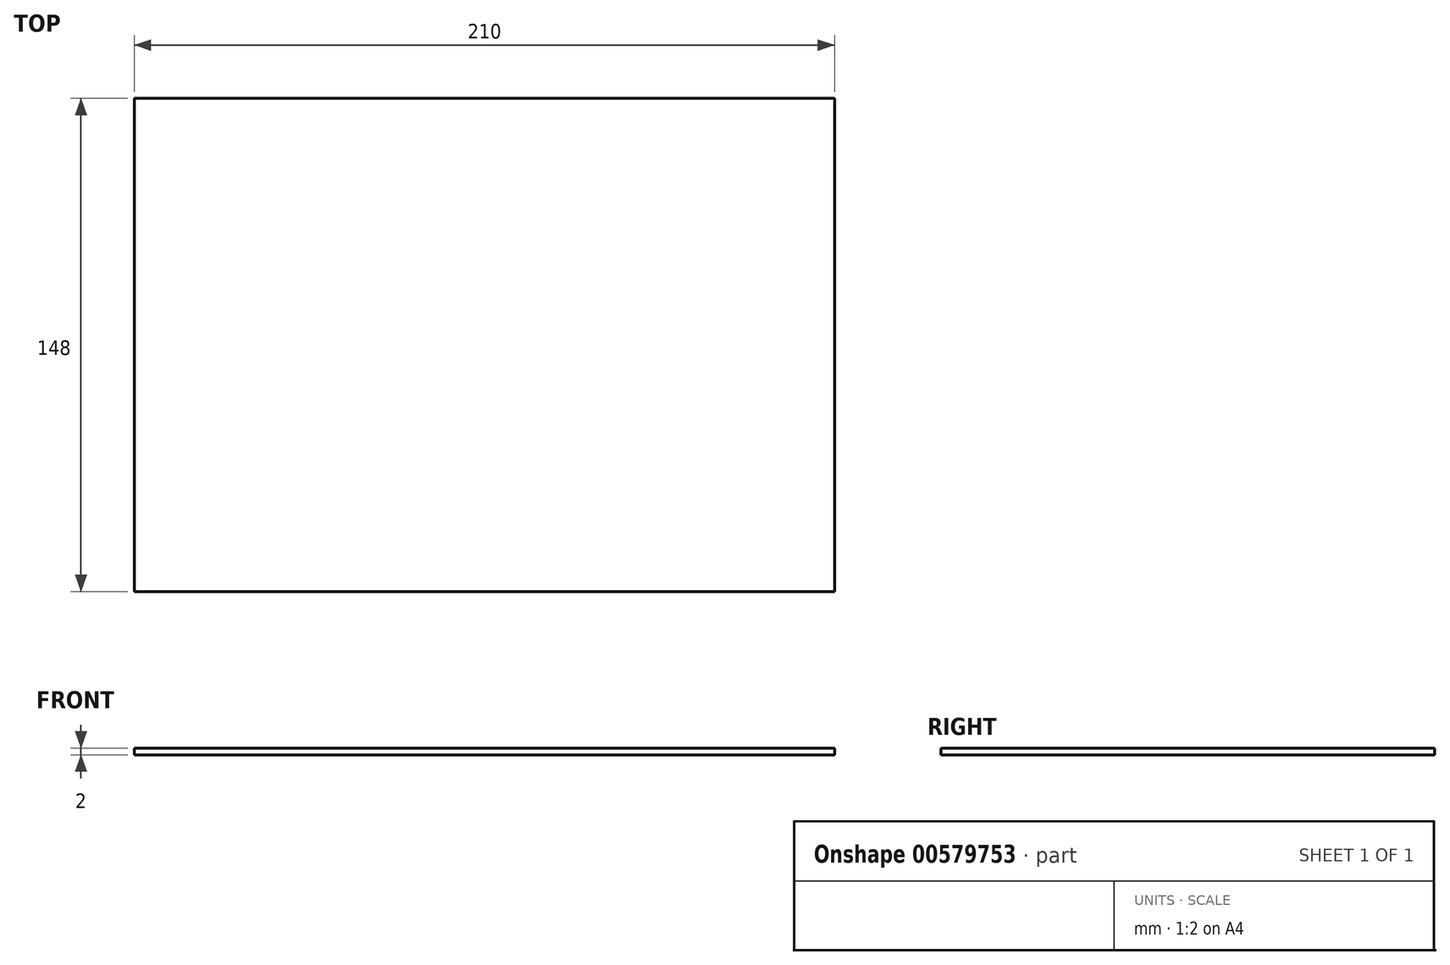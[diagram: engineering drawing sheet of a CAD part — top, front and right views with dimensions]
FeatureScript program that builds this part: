
annotation { "Feature Type Name" : "Feature", "Feature Type Description" : "" }
export const myFeature = defineFeature(function(context is Context, id is Id, definition is map)
    precondition{}
    {
        {
            var Q0;
            Q0=qCreatedBy(makeId("Top.planeOp"),FACE);
            var sketch = newSketch(context, id + "F0", { "sketchPlane" : qUnion([Q0])});
            skLineSegment(sketch, "E0.bottom", {"start": v(-51.26, 44.59) * mm, "end": v(-261.26, 44.59) * mm});
            skLineSegment(sketch, "E0.top", {"start": v(-51.26, 192.59) * mm, "end": v(-261.26, 192.59) * mm});
            skLineSegment(sketch, "E0.left", {"start": v(-51.26, 44.59) * mm, "end": v(-51.26, 192.59) * mm});
            skLineSegment(sketch, "E0.right", {"start": v(-261.26, 44.59) * mm, "end": v(-261.26, 192.59) * mm});
            skSolve(sketch);
        }
        {
            var Q0;
            Q0 = qSketchRegion(id + "F0", true);
            extrude(context, id + "F1", {"entities" : qUnion([Q0]), "depth" : 2 * mm, "offsetDistance" : 25 * mm});
        }
    });
